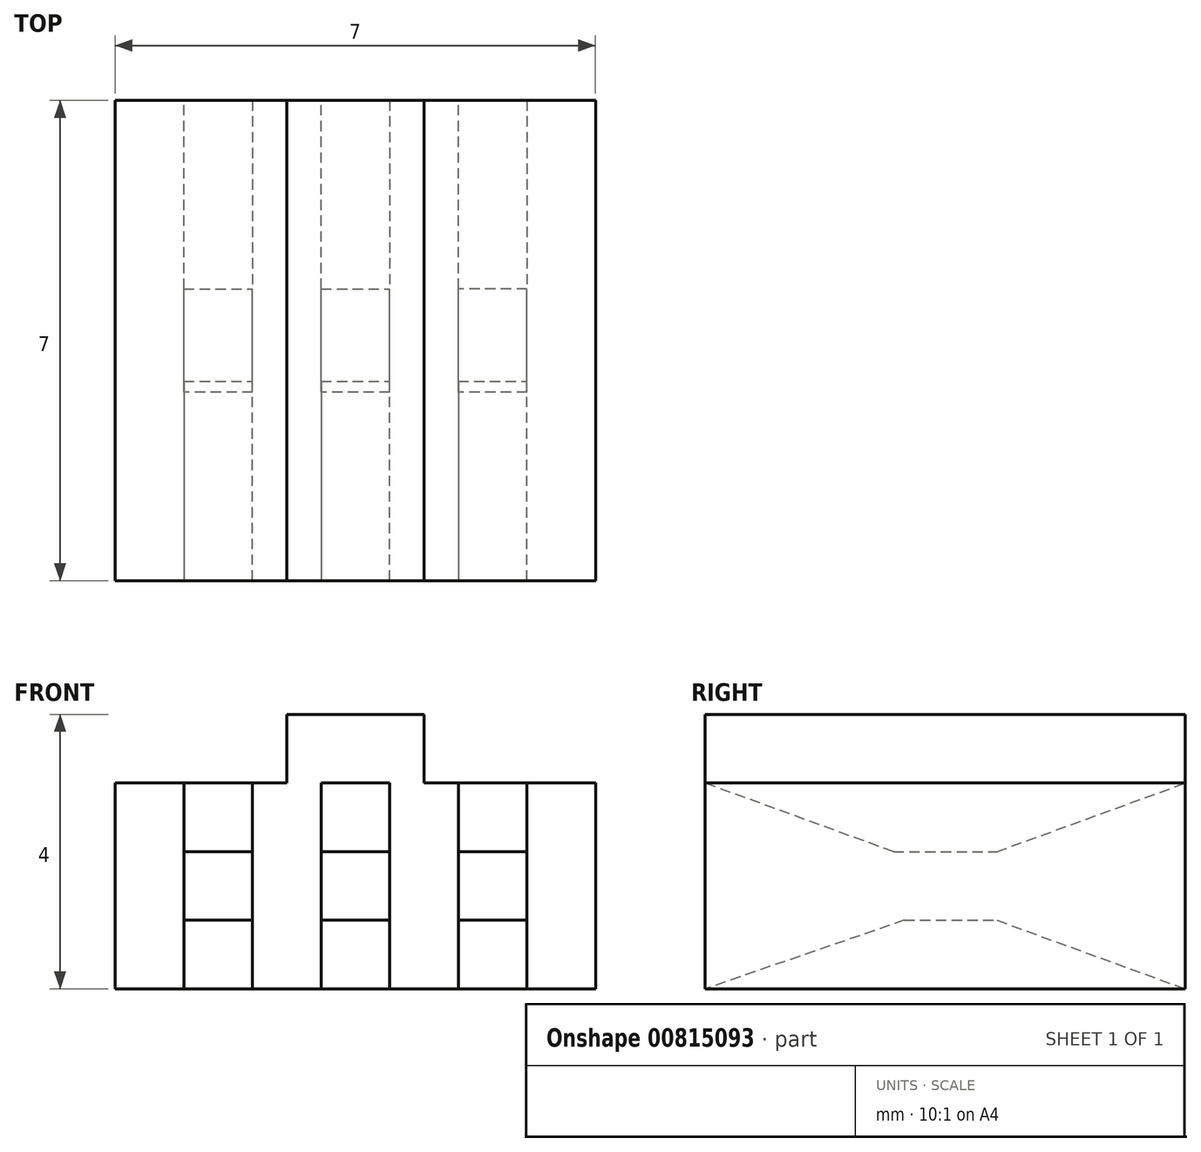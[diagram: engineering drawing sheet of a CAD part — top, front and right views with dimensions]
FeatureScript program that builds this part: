
annotation { "Feature Type Name" : "Feature", "Feature Type Description" : "" }
export const myFeature = defineFeature(function(context is Context, id is Id, definition is map)
    precondition{}
    {
        {
            var Q0;
            Q0=qCreatedBy(makeId("Front.planeOp"),FACE);
            var sketch = newSketch(context, id + "F0", { "sketchPlane" : qUnion([Q0])});
            skLineSegment(sketch, "E0.bottom", {"start": v(-61.89, 15.68) * mm, "end": v(-59.89, 15.68) * mm});
            skLineSegment(sketch, "E0.top", {"start": v(-61.89, 14.68) * mm, "end": v(-59.89, 14.68) * mm});
            skLineSegment(sketch, "E0.left", {"start": v(-61.89, 15.68) * mm, "end": v(-61.89, 14.68) * mm});
            skLineSegment(sketch, "E0.right", {"start": v(-59.89, 15.68) * mm, "end": v(-59.89, 14.68) * mm});
            skLineSegment(sketch, "E1.top", {"start": v(-55.75, 26.29) * mm, "end": v(-54.75, 26.29) * mm});
            skLineSegment(sketch, "E2.top", {"start": v(-55.75, 27.29) * mm, "end": v(-54.75, 27.29) * mm});
            skLineSegment(sketch, "E3.bottom", {"start": v(-53.75, 27.29) * mm, "end": v(-52.75, 27.29) * mm});
            skLineSegment(sketch, "E3.top", {"start": v(-53.75, 26.29) * mm, "end": v(-52.75, 26.29) * mm});
            skLineSegment(sketch, "E3.left", {"start": v(-53.75, 27.29) * mm, "end": v(-53.75, 26.29) * mm});
            skLineSegment(sketch, "E3.right", {"start": v(-52.75, 27.29) * mm, "end": v(-52.75, 26.29) * mm});
            skLineSegment(sketch, "E4.bottom", {"start": v(-51.75, 27.29) * mm, "end": v(-50.75, 27.29) * mm});
            skLineSegment(sketch, "E4.top", {"start": v(-51.75, 26.29) * mm, "end": v(-50.75, 26.29) * mm});
            skLineSegment(sketch, "E4.left", {"start": v(-51.75, 27.29) * mm, "end": v(-51.75, 26.29) * mm});
            skLineSegment(sketch, "E4.right", {"start": v(-50.75, 27.29) * mm, "end": v(-50.75, 26.29) * mm});
            skLineSegment(sketch, "E5", {"start": v(-50.75, 26.79) * mm, "end": v(-49.75, 26.79) * mm});
            skLineSegment(sketch, "E6", {"start": v(-54.75, 26.29) * mm, "end": v(-54.75, 27.29) * mm});
            skLineSegment(sketch, "E7", {"start": v(-55.75, 27.29) * mm, "end": v(-55.75, 26.29) * mm});
            skLineSegment(sketch, "E8", {"start": v(-55.75, 26.79) * mm, "end": v(-56.75, 26.79) * mm});
            skLineSegment(sketch, "E9", {"start": v(-51.25, 27.29) * mm, "end": v(-51.25, 28.29) * mm});
            skLineSegment(sketch, "E10", {"start": v(-51.25, 26.29) * mm, "end": v(-51.25, 25.29) * mm});
            skLineSegment(sketch, "E11.bottom", {"start": v(-49.75, 28.29) * mm, "end": v(-56.75, 28.29) * mm});
            skLineSegment(sketch, "E11.top", {"start": v(-49.75, 25.29) * mm, "end": v(-56.75, 25.29) * mm});
            skLineSegment(sketch, "E11.left", {"start": v(-49.75, 28.29) * mm, "end": v(-49.75, 25.29) * mm});
            skLineSegment(sketch, "E11.right", {"start": v(-56.75, 28.29) * mm, "end": v(-56.75, 25.29) * mm});
            skLineSegment(sketch, "E12", {"start": v(-53.25, 28.29) * mm, "end": v(-53.25, 29.29) * mm});
            skLineSegment(sketch, "E13", {"start": v(-53.25, 29.29) * mm, "end": v(-54.25, 29.29) * mm});
            skLineSegment(sketch, "E14", {"start": v(-54.25, 29.29) * mm, "end": v(-53.25, 29.29) * mm});
            skLineSegment(sketch, "E15", {"start": v(-53.25, 29.29) * mm, "end": v(-52.25, 29.29) * mm});
            skLineSegment(sketch, "E16", {"start": v(-52.25, 28.29) * mm, "end": v(-52.25, 29.29) * mm});
            skLineSegment(sketch, "E17", {"start": v(-54.25, 29.29) * mm, "end": v(-54.25, 28.29) * mm});
            skSolve(sketch);
        }
        {
            var Q0;
            {var subQ11=sQuery(id+"F0.wireOp",EDGE,"E1.top");Q0=makeQuery(id+"F0.imprint","IMPRINT",FACE,{"disambiguationData":[TD([[makeQuery(id+"F0.imprint","IMPRINT",EDGE,{"derivedFrom":subQ11}),-1.0]])]});}
            var Q1;
            {var subQ0=sQuery(id+"F0.wireOp",EDGE,"E5");Q1=makeQuery(id+"F0.imprint","IMPRINT",FACE,{"disambiguationData":[TD([[makeQuery(id+"F0.imprint","IMPRINT",EDGE,{"derivedFrom":subQ0}),1.0]])]});}
            var Q2;
            {var subQ1=sQuery(id+"F0.wireOp",EDGE,"E5");Q2=makeQuery(id+"F0.imprint","IMPRINT",FACE,{"disambiguationData":[TD([[makeQuery(id+"F0.imprint","IMPRINT",EDGE,{"derivedFrom":subQ1}),-1.0]])]});}
            var Q3;
            {var subQ0=sQuery(id+"F0.wireOp",EDGE,"E12");Q3=makeQuery(id+"F0.imprint","IMPRINT",FACE,{"disambiguationData":[TD([[makeQuery(id+"F0.imprint","IMPRINT",EDGE,{"derivedFrom":subQ0}),-1.0]])]});}
            var Q4;
            {var subQ0=sQuery(id+"F0.wireOp",EDGE,"E12");Q4=makeQuery(id+"F0.imprint","IMPRINT",FACE,{"disambiguationData":[TD([[makeQuery(id+"F0.imprint","IMPRINT",EDGE,{"derivedFrom":subQ0}),1.0]])]});}
            extrude(context, id + "F1", {"entities" : qUnion([Q0, Q1, Q2, Q3, Q4]), "depth" : 7 * mm, "offsetDistance" : 25 * mm});
        }
        {
            var Q0;
            Q0=makeQuery(id+"F1.opExtrude","CAP_EDGE",EDGE,{"disambiguationData":[OSD([sQuery(id+"F0.wireOp",EDGE,"E4.top")])],"isStart":true});
            var Q1;
            Q1=makeQuery(id+"F1.opExtrude","CAP_EDGE",EDGE,{"disambiguationData":[OSD([sQuery(id+"F0.wireOp",EDGE,"E4.bottom")])],"isStart":true});
            var Q2;
            Q2=makeQuery(id+"F1.opExtrude","CAP_EDGE",EDGE,{"disambiguationData":[OSD([sQuery(id+"F0.wireOp",EDGE,"E3.bottom")])],"isStart":true});
            var Q3;
            Q3=makeQuery(id+"F1.opExtrude","CAP_EDGE",EDGE,{"disambiguationData":[OSD([sQuery(id+"F0.wireOp",EDGE,"E3.top")])],"isStart":true});
            var Q4;
            Q4=makeQuery(id+"F1.opExtrude","CAP_EDGE",EDGE,{"disambiguationData":[OSD([sQuery(id+"F0.wireOp",EDGE,"E2.top")])],"isStart":true});
            var Q5;
            Q5=makeQuery(id+"F1.opExtrude","CAP_EDGE",EDGE,{"disambiguationData":[OSD([sQuery(id+"F0.wireOp",EDGE,"E1.top")])],"isStart":true});
            var Q6;
            Q6=makeQuery(id+"F1.opExtrude","CAP_EDGE",EDGE,{"disambiguationData":[OSD([sQuery(id+"F0.wireOp",EDGE,"E2.top")])],"isStart":false});
            var Q7;
            Q7=makeQuery(id+"F1.opExtrude","CAP_EDGE",EDGE,{"disambiguationData":[OSD([sQuery(id+"F0.wireOp",EDGE,"E3.bottom")])],"isStart":false});
            var Q8;
            Q8=makeQuery(id+"F1.opExtrude","CAP_EDGE",EDGE,{"disambiguationData":[OSD([sQuery(id+"F0.wireOp",EDGE,"E4.bottom")])],"isStart":false});
            chamfer(context, id + "F2", {"entities" : qUnion([Q0, Q1, Q2, Q3, Q4, Q5, Q6, Q7, Q8]), "chamferType" : ChamferType.OFFSET_ANGLE, "width" : 1 * mm, "oppositeDirection" : false, "angle" : 70 * degree, "tangentPropagation" : true});
        }
        {
            var Q0;
            Q0=makeQuery(id+"F1.opExtrude","CAP_EDGE",EDGE,{"disambiguationData":[OSD([sQuery(id+"F0.wireOp",EDGE,"E1.top")])],"isStart":false});
            var Q1;
            Q1=makeQuery(id+"F1.opExtrude","CAP_EDGE",EDGE,{"disambiguationData":[OSD([sQuery(id+"F0.wireOp",EDGE,"E3.top")])],"isStart":false});
            var Q2;
            Q2=makeQuery(id+"F1.opExtrude","CAP_EDGE",EDGE,{"disambiguationData":[OSD([sQuery(id+"F0.wireOp",EDGE,"E4.top")])],"isStart":false});
            chamfer(context, id + "F3", {"entities" : qUnion([Q0, Q1, Q2]), "chamferType" : ChamferType.OFFSET_ANGLE, "width" : 1 * mm, "oppositeDirection" : true, "angle" : 71 * degree, "tangentPropagation" : true});
        }
    });
